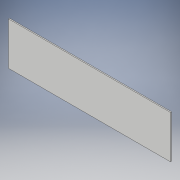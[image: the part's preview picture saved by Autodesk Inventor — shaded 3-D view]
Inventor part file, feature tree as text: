
AUTODESK INVENTOR PART (.ipt)
format: ipt  version: 2017 (Build 210142000, 142)  size: 88,064 bytes
history: native  units: in
note: dims shown in document units (in); Inventor stores cm internally (conversion verified against a paired STEP export)
features: extrude x1, sketch x1
ambient origin geometry x8: Origin, YZ Plane, XZ Plane, XY Plane, X Axis, Y Axis, Z Axis, Center Point
bodies: Solid1 (feature_tree)
feature tree (2):
  extrude  "Extrusion1"  Depth=19.0in
  sketch  "Sketch1"  dims[d0=72.0in d1=19.0in d2=0.5in d3=0.0in]
